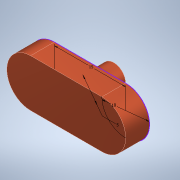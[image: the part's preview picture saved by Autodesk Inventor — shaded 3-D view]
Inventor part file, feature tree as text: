
AUTODESK INVENTOR PART (.ipt)
format: ipt  version: 2022 (Build 260153000, 153)  size: 109,568 bytes
history: native  units: mm
features: extrude x2, sketch x1
ambient origin geometry x8: Origin, YZ Plane, XZ Plane, XY Plane, X Axis, Y Axis, Z Axis, Center Point
bodies: Body1 (feature_tree)
feature tree (3):
  sketch  "Sketch1"  dims[d0=10.0mm d1=5.0mm d7=5.0mm d8=0.0mm d9=5.0mm d10=0.0mm d11=15.0mm]
  extrude  "Extrusion3"  Depth=5.0mm
  extrude  "Extrusion4"  Depth=5.0mm TaperAngle=0.0deg
